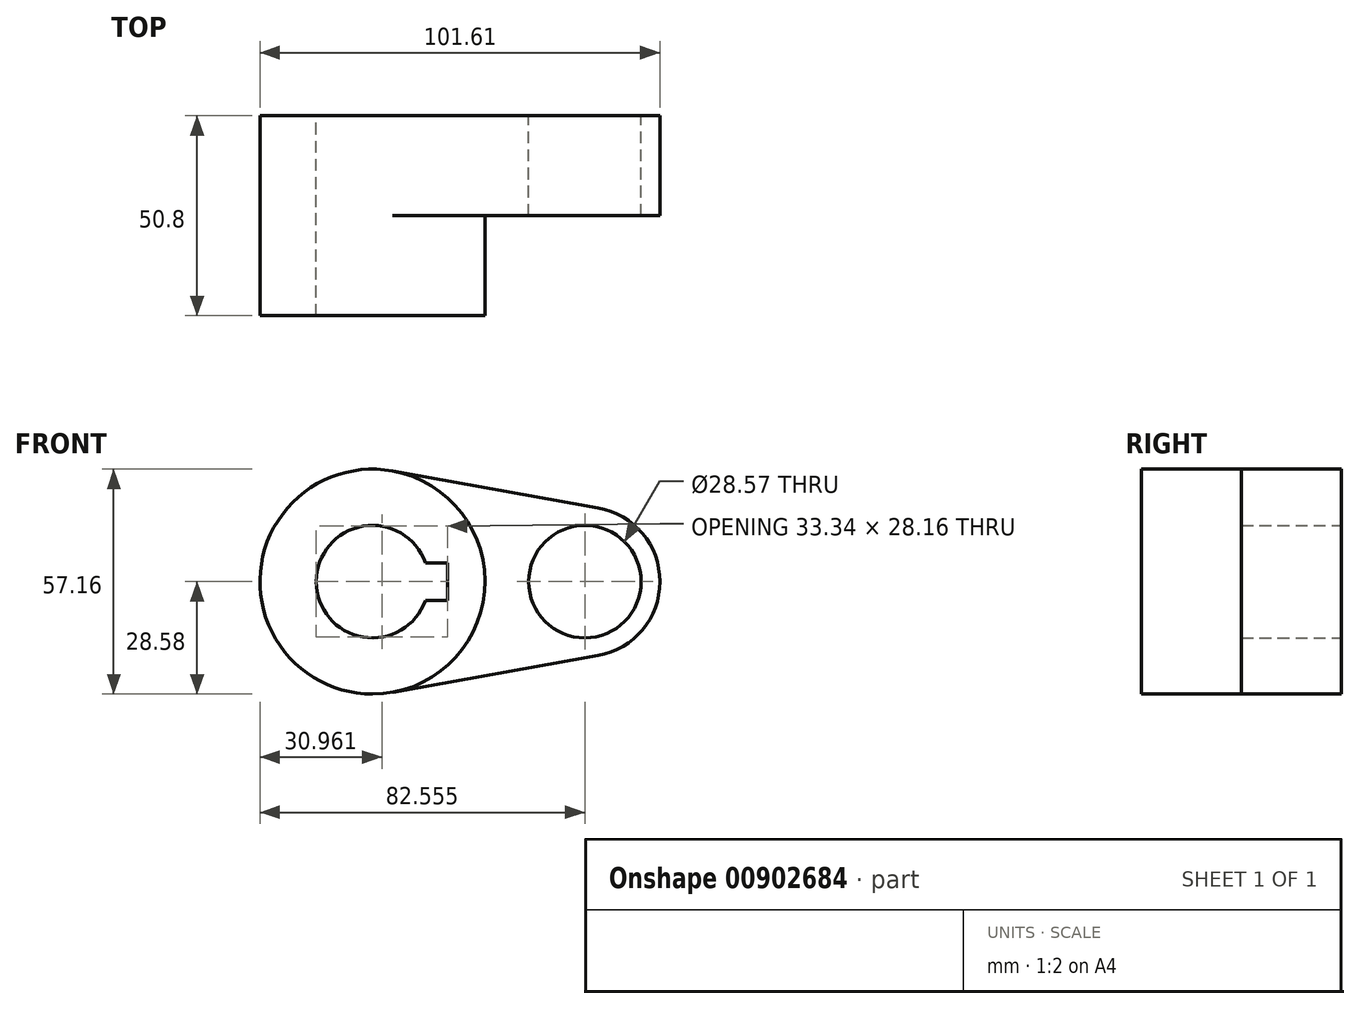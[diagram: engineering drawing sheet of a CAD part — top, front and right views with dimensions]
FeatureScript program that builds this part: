
annotation { "Feature Type Name" : "Feature", "Feature Type Description" : "" }
export const myFeature = defineFeature(function(context is Context, id is Id, definition is map)
    precondition{}
    {
        {
            var Q0;
            Q0=qCreatedBy(makeId("Front.planeOp"),FACE);
            var sketch = newSketch(context, id + "F0", { "sketchPlane" : qUnion([Q0])});
            skCircle(sketch, "E0", {"center": v(0, 0) * mm, "radius": 28.58 * mm});
            skCircle(sketch, "E1", {"center": v(53.98, 0) * mm, "radius": 19.05 * mm});
            skLineSegment(sketch, "E2", {"start": v(5.04, 28.13) * mm, "end": v(57.34, 18.75) * mm});
            skLineSegment(sketch, "E3", {"start": v(5.04, -28.13) * mm, "end": v(57.34, -18.75) * mm});
            skCircle(sketch, "E4", {"center": v(0, 0) * mm, "radius": 14.29 * mm});
            skCircle(sketch, "E5", {"center": v(53.98, 0) * mm, "radius": 14.29 * mm});
            skLineSegment(sketch, "E6.bottom", {"start": v(19.05, -4.76) * mm, "end": v(-19.05, -4.76) * mm});
            skLineSegment(sketch, "E6.top", {"start": v(19.05, 4.76) * mm, "end": v(-19.05, 4.76) * mm});
            skLineSegment(sketch, "E6.left", {"start": v(19.05, -4.76) * mm, "end": v(19.05, 4.76) * mm});
            skLineSegment(sketch, "E6.right", {"start": v(-19.05, -4.76) * mm, "end": v(-19.05, 4.76) * mm});
            skSolve(sketch);
        }
        {
            var Q0;
            {var subQ5=sQuery(id+"F0.wireOp",EDGE,"E6.right");Q0=makeQuery(id+"F0.imprint","IMPRINT",FACE,{"disambiguationData":[TD([[makeQuery(id+"F0.imprint","IMPRINT",EDGE,{"derivedFrom":subQ5}),-1.0]])]});}
            var Q1;
            {var subQ7=sQuery(id+"F0.wireOp",EDGE,"E6.left");Q1=makeQuery(id+"F0.imprint","IMPRINT",FACE,{"disambiguationData":[TD([[makeQuery(id+"F0.imprint","IMPRINT",EDGE,{"derivedFrom":subQ7}),-1.0]])]});}
            var Q2;
            {var subQ0=sQuery(id+"F0.wireOp",EDGE,"E2");Q2=makeQuery(id+"F0.imprint","IMPRINT",FACE,{"disambiguationData":[TD([[makeQuery(id+"F0.imprint","IMPRINT",EDGE,{"derivedFrom":subQ0}),-1.0]])]});}
            var Q3;
            Q3=makeQuery(id+"F0.imprint","IMPRINT",FACE,{"disambiguationData":[TD([[makeQuery(id+"F0.imprint","IMPRINT",EDGE,{"derivedFrom":sQuery(id+"F0.wireOp",EDGE,"E5")}),-1.0]])]});
            extrude(context, id + "F1", {"entities" : qUnion([Q0, Q1, Q2, Q3]), "depth" : 25.4 * mm, "offsetDistance" : 25.4 * mm});
        }
        {
            var Q0;
            {var subQ7=sQuery(id+"F0.wireOp",EDGE,"E6.left");Q0=makeQuery(id+"F0.imprint","IMPRINT",FACE,{"disambiguationData":[TD([[makeQuery(id+"F0.imprint","IMPRINT",EDGE,{"derivedFrom":subQ7}),-1.0]])]});}
            var Q1;
            {var subQ5=sQuery(id+"F0.wireOp",EDGE,"E6.right");Q1=makeQuery(id+"F0.imprint","IMPRINT",FACE,{"disambiguationData":[TD([[makeQuery(id+"F0.imprint","IMPRINT",EDGE,{"derivedFrom":subQ5}),-1.0]])]});}
            extrude(context, id + "F2", {"entities" : qUnion([Q0, Q1]), "operationType" : NewBodyOperationType.ADD, "depth" : 50.8 * mm, "offsetDistance" : 25.4 * mm});
        }
    });
